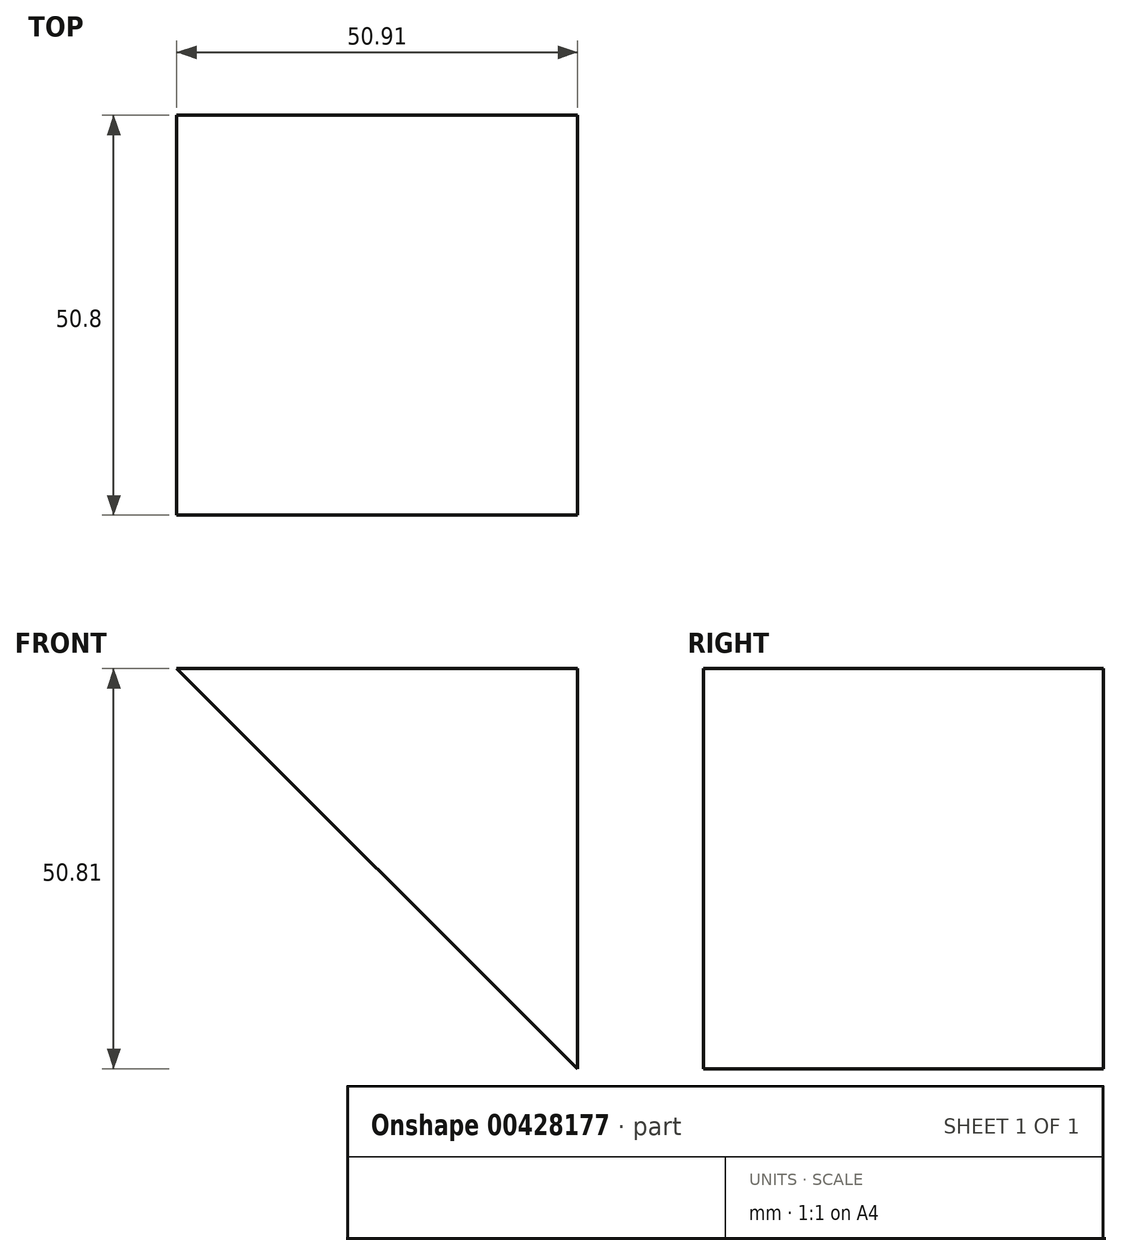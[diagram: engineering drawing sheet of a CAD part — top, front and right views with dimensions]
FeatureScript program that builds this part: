
annotation { "Feature Type Name" : "Feature", "Feature Type Description" : "" }
export const myFeature = defineFeature(function(context is Context, id is Id, definition is map)
    precondition{}
    {
        {
            var Q0;
            Q0=qCreatedBy(makeId("Front.planeOp"),FACE);
            var sketch = newSketch(context, id + "F0", { "sketchPlane" : qUnion([Q0])});
            skLineSegment(sketch, "E0", {"start": v(0, 0) * mm, "end": v(0, 50.81) * mm});
            skLineSegment(sketch, "E1", {"start": v(0, 50.81) * mm, "end": v(-50.9, 50.81) * mm});
            skLineSegment(sketch, "E2", {"start": v(-50.9, 50.81) * mm, "end": v(0, 0) * mm});
            skSolve(sketch);
        }
        {
            var Q0;
            Q0 = qSketchRegion(id + "F0", true);
            extrude(context, id + "F1", {"entities" : qUnion([Q0]), "depth" : 50.8 * mm});
        }
    });
